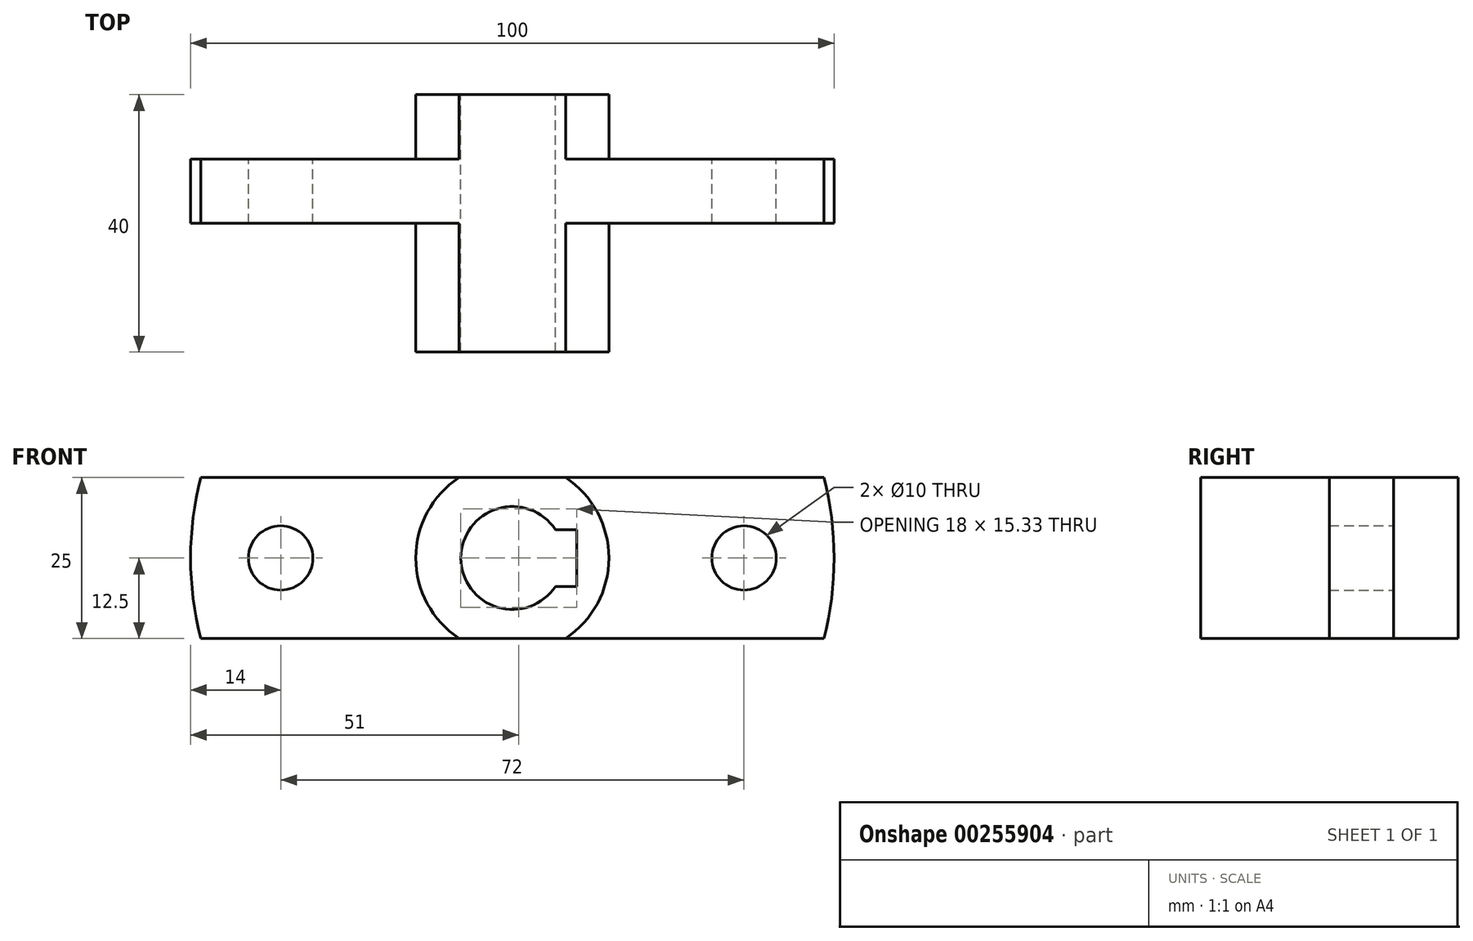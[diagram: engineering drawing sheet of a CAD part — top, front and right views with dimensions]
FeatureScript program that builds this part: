
annotation { "Feature Type Name" : "Feature", "Feature Type Description" : "" }
export const myFeature = defineFeature(function(context is Context, id is Id, definition is map)
    precondition{}
    {
        {
            var Q0;
            Q0=qCreatedBy(makeId("Front.planeOp"),FACE);
            var sketch = newSketch(context, id + "F0", { "sketchPlane" : qUnion([Q0])});
            skArc(sketch, "E0", {"start": v(0, -8) * mm, "mid": v(8, 0) * mm, "end": v(0, 8) * mm});
            skLineSegment(sketch, "E1.bottom", {"start": v(48.41, 12.5) * mm, "end": v(0, 12.5) * mm});
            skLineSegment(sketch, "E1.top", {"start": v(48.41, -12.5) * mm, "end": v(0, -12.5) * mm});
            skCircle(sketch, "E2", {"center": v(36, 0) * mm, "radius": 5 * mm});
            skArc(sketch, "E3.trimOffspring", {"start": v(8.3, -12.5) * mm, "mid": v(15, 0) * mm, "end": v(8.3, 12.5) * mm});
            skArc(sketch, "E4", {"start": v(48.41, 12.5) * mm, "mid": v(50, 0) * mm, "end": v(48.41, -12.5) * mm});
            skLineSegment(sketch, "E5", {"start": v(0, 12.5) * mm, "end": v(0, -12.5) * mm});
            skPoint(sketch, "E1.right.start.orphan", {"position": v(-48.41, 12.5) * mm});
            skPoint(sketch, "E6.orphan", {"position": v(-48.41, -12.5) * mm});
            skSolve(sketch);
        }
        {
            var Q0;
            {var subQ6=sQuery(id+"F0.wireOp",EDGE,"E0");Q0=makeQuery(id+"F0.imprint","IMPRINT",FACE,{"disambiguationData":[TD([[makeQuery(id+"F0.imprint","IMPRINT",EDGE,{"derivedFrom":subQ6}),-1.0]])]});}
            extrude(context, id + "F1", {"entities" : qUnion([Q0]), "depth" : 30 * mm, "hasSecondDirection" : true, "secondDirectionOppositeDirection" : true, "secondDirectionDepth" : 10 * mm});
        }
        {
            var Q0;
            Q0=makeQuery(id+"F0.imprint","IMPRINT",FACE,{"disambiguationData":[TD([[makeQuery(id+"F0.imprint","IMPRINT",EDGE,{"derivedFrom":sQuery(id+"F0.wireOp",EDGE,"E2")}),-1.0]])]});
            extrude(context, id + "F2", {"entities" : qUnion([Q0]), "operationType" : NewBodyOperationType.ADD, "depth" : 10 * mm});
        }
        {
            var Q0;
            Q0=makeQuery(id+"F1.opExtrude","SWEPT_BODY",BODY,{"disambiguationData":[OSD([sQuery(id+"F0.wireOp",EDGE,"E0"),sQuery(id+"F0.wireOp",EDGE,"E1.bottom"),sQuery(id+"F0.wireOp",EDGE,"E1.top"),sQuery(id+"F0.wireOp",EDGE,"E3.trimOffspring"),sQuery(id+"F0.wireOp",EDGE,"E5")])]});
            var Q1;
            Q1=qCreatedBy(makeId("Right.planeOp"),FACE);
            mirror(context, id + "F3", {"operationType" : NewBodyOperationType.ADD, "entities" : qUnion([Q0]), "mirrorPlane" : qUnion([Q1])});
        }
        {
            var Q0;
            {var subQ0=makeQuery(id+"F1.opExtrude","CAP_FACE",FACE,{"disambiguationData":[OSD([sQuery(id+"F0.wireOp",EDGE,"E0"),sQuery(id+"F0.wireOp",EDGE,"E1.bottom"),sQuery(id+"F0.wireOp",EDGE,"E1.top"),sQuery(id+"F0.wireOp",EDGE,"E3.trimOffspring"),sQuery(id+"F0.wireOp",EDGE,"E5")])],"isStart":true});Q0=makeQuery(id+"F3.boolean.opBoolean","MERGE",FACE,{"derivedFrom":[subQ0,makeQuery(id+"F3.opPattern","COPY",FACE,{"derivedFrom":subQ0,"instanceName":"1"})]});}
            var sketch = newSketch(context, id + "F4", { "sketchPlane" : qUnion([Q0])});
            skLineSegment(sketch, "E7.0.0", {"start": v(8.3, 12.5) * mm, "end": v(-8.3, 12.5) * mm});
            skArc(sketch, "E7.0.1", {"start": v(-8.3, 12.5) * mm, "mid": v(-15, 0) * mm, "end": v(-8.3, -12.5) * mm});
            skLineSegment(sketch, "E7.0.2", {"start": v(-8.3, -12.5) * mm, "end": v(8.3, -12.5) * mm});
            skArc(sketch, "E7.0.3", {"start": v(8.3, -12.5) * mm, "mid": v(15, 0) * mm, "end": v(8.3, 12.5) * mm});
            skLineSegment(sketch, "E8.bottom", {"start": v(-10, 4.4) * mm, "end": v(-2.17, 4.4) * mm});
            skLineSegment(sketch, "E8.top", {"start": v(-10, -4.4) * mm, "end": v(-2.17, -4.4) * mm});
            skLineSegment(sketch, "E8.left", {"start": v(-10, 4.4) * mm, "end": v(-10, -4.4) * mm});
            skLineSegment(sketch, "E8.right", {"start": v(-2.17, 4.4) * mm, "end": v(-2.17, -4.4) * mm});
            skPoint(sketch, "E8.middle", {"position": v(-6.09, 0) * mm});
            skPoint(sketch, "E8.middle.positionSnap0", {"position": v(-15, 0) * mm});
            skPoint(sketch, "E8.centerSnap0", {"position": v(-15, 0) * mm});
            skPoint(sketch, "E9", {"position": v(8, 0) * mm});
            skSolve(sketch);
        }
        {
            var Q0;
            {var subQ0=sQuery(id+"F4.wireOp",EDGE,"E8.left");Q0=makeQuery(id+"F4.imprint","IMPRINT",FACE,{"disambiguationData":[TD([[makeQuery(id+"F4.imprint","IMPRINT",EDGE,{"derivedFrom":subQ0}),1.0]])]});}
            extrude(context, id + "F5", {"entities" : qUnion([Q0]), "operationType" : NewBodyOperationType.REMOVE, "endBound" : BoundingType.THROUGH_ALL, "oppositeDirection" : true, "depth" : 25 * mm});
        }
    });
